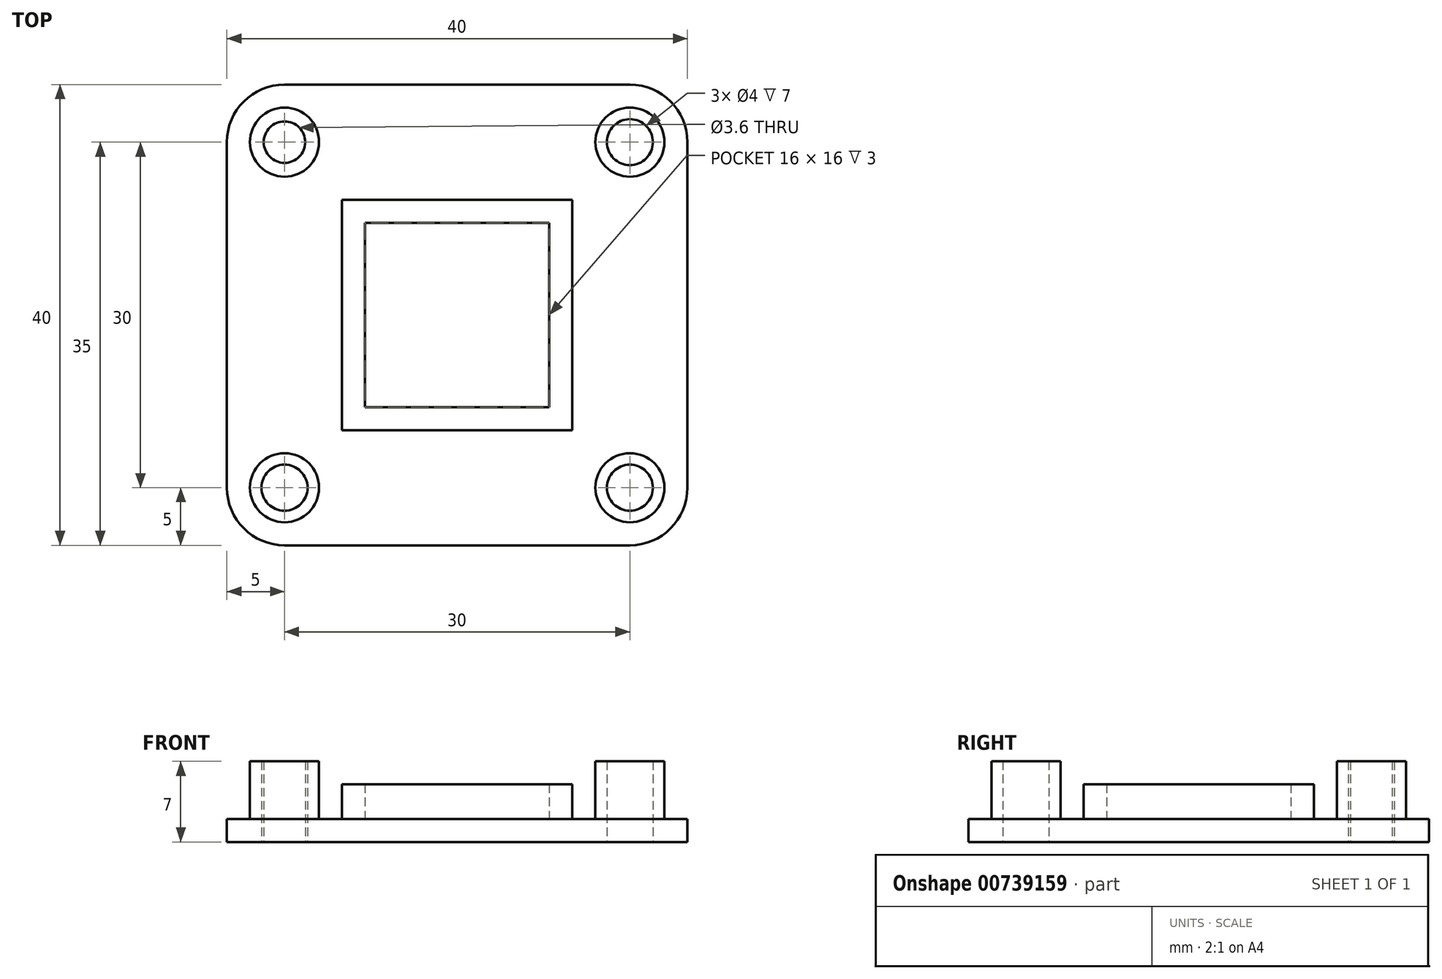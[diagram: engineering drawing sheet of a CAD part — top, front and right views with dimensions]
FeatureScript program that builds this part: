
annotation { "Feature Type Name" : "Feature", "Feature Type Description" : "" }
export const myFeature = defineFeature(function(context is Context, id is Id, definition is map)
    precondition{}
    {
        {
            var Q0;
            Q0=qCreatedBy(makeId("Top.planeOp"),FACE);
            var sketch = newSketch(context, id + "F0", { "sketchPlane" : qUnion([Q0])});
            skLineSegment(sketch, "E0.bottom", {"start": v(15, -20) * mm, "end": v(-15, -20) * mm});
            skLineSegment(sketch, "E0.top", {"start": v(15, 20) * mm, "end": v(-15, 20) * mm});
            skLineSegment(sketch, "E0.left", {"start": v(20, -15) * mm, "end": v(20, 15) * mm});
            skLineSegment(sketch, "E0.right", {"start": v(-20, -15) * mm, "end": v(-20, 15) * mm});
            skPoint(sketch, "E0.middle", {"position": v(0, 0) * mm});
            skCircle(sketch, "E1", {"center": v(-15, -15) * mm, "radius": 2 * mm});
            skCircle(sketch, "E2", {"center": v(-15, 15) * mm, "radius": 1.8 * mm});
            skCircle(sketch, "E3", {"center": v(15, -15) * mm, "radius": 2 * mm});
            skCircle(sketch, "E4", {"center": v(15, 15) * mm, "radius": 2 * mm});
            skPoint(sketch, "E5.visualSharp", {"position": v(-20, 20) * mm});
            skArc(sketch, "E5.filletArc", {"start": v(-15, 20) * mm, "mid": v(-18.54, 18.54) * mm, "end": v(-20, 15) * mm});
            skPoint(sketch, "E6.visualSharp", {"position": v(20, 20) * mm});
            skArc(sketch, "E6.filletArc", {"start": v(20, 15) * mm, "mid": v(18.54, 18.54) * mm, "end": v(15, 20) * mm});
            skPoint(sketch, "E7.visualSharp", {"position": v(20, -20) * mm});
            skArc(sketch, "E7.filletArc", {"start": v(15, -20) * mm, "mid": v(18.54, -18.54) * mm, "end": v(20, -15) * mm});
            skPoint(sketch, "E8.visualSharp", {"position": v(-20, -20) * mm});
            skArc(sketch, "E8.filletArc", {"start": v(-20, -15) * mm, "mid": v(-18.54, -18.54) * mm, "end": v(-15, -20) * mm});
            skSolve(sketch);
        }
        {
            var Q0;
            Q0=makeQuery(id+"F0.imprint","IMPRINT",FACE,{"disambiguationData":[TD([[makeQuery(id+"F0.imprint","IMPRINT",EDGE,{"derivedFrom":sQuery(id+"F0.wireOp",EDGE,"E0.bottom")}),-1.0]])]});
            var Q1;
            Q1=makeQuery(id+"F0.imprint","IMPRINT",FACE,{"disambiguationData":[TD([[makeQuery(id+"F0.imprint","IMPRINT",EDGE,{"derivedFrom":sQuery(id+"F0.wireOp",EDGE,"E4")}),-1.0]])]});
            var Q2;
            Q2=makeQuery(id+"F0.imprint","IMPRINT",FACE,{"disambiguationData":[TD([[makeQuery(id+"F0.imprint","IMPRINT",EDGE,{"derivedFrom":sQuery(id+"F0.wireOp",EDGE,"E2")}),-1.0]])]});
            var Q3;
            Q3=makeQuery(id+"F0.imprint","IMPRINT",FACE,{"disambiguationData":[TD([[makeQuery(id+"F0.imprint","IMPRINT",EDGE,{"derivedFrom":sQuery(id+"F0.wireOp",EDGE,"E1")}),-1.0]])]});
            var Q4;
            Q4=makeQuery(id+"F0.imprint","IMPRINT",FACE,{"disambiguationData":[TD([[makeQuery(id+"F0.imprint","IMPRINT",EDGE,{"derivedFrom":sQuery(id+"F0.wireOp",EDGE,"E3")}),-1.0]])]});
            extrude(context, id + "F1", {"entities" : qUnion([Q0, Q1, Q2, Q3, Q4]), "depth" : 2 * mm, "offsetDistance" : 25 * mm});
        }
        {
            var Q0;
            Q0=makeQuery(id+"F1.opExtrude","CAP_FACE",FACE,{"disambiguationData":[OSD([sQuery(id+"F0.wireOp",EDGE,"E0.bottom"),sQuery(id+"F0.wireOp",EDGE,"E0.top"),sQuery(id+"F0.wireOp",EDGE,"E0.left"),sQuery(id+"F0.wireOp",EDGE,"E0.right"),sQuery(id+"F0.wireOp",EDGE,"E1"),sQuery(id+"F0.wireOp",EDGE,"E2"),sQuery(id+"F0.wireOp",EDGE,"E3"),sQuery(id+"F0.wireOp",EDGE,"E4")])],"isStart":false});
            var sketch = newSketch(context, id + "F2", { "sketchPlane" : qUnion([Q0])});
            skCircle(sketch, "E9.0", {"center": v(-15, 15) * mm, "radius": 1.8 * mm});
            skCircle(sketch, "E9.1", {"center": v(15, 15) * mm, "radius": 2 * mm});
            skCircle(sketch, "E9.2", {"center": v(15, -15) * mm, "radius": 2 * mm});
            skCircle(sketch, "E9.3", {"center": v(-15, -15) * mm, "radius": 2 * mm});
            skCircle(sketch, "E10", {"center": v(-15, 15) * mm, "radius": 3 * mm});
            skCircle(sketch, "E11", {"center": v(15, 15) * mm, "radius": 3 * mm});
            skCircle(sketch, "E12", {"center": v(15, -15) * mm, "radius": 3 * mm});
            skCircle(sketch, "E13", {"center": v(-15, -15) * mm, "radius": 3 * mm});
            skSolve(sketch);
        }
        {
            var Q0;
            Q0=makeQuery(id+"F2.imprint","IMPRINT",FACE,{"disambiguationData":[TD([[makeQuery(id+"F2.imprint","IMPRINT",EDGE,{"derivedFrom":sQuery(id+"F2.wireOp",EDGE,"E9.0")}),-1.0]])]});
            var Q1;
            Q1=makeQuery(id+"F2.imprint","IMPRINT",FACE,{"disambiguationData":[TD([[makeQuery(id+"F2.imprint","IMPRINT",EDGE,{"derivedFrom":sQuery(id+"F2.wireOp",EDGE,"E9.1")}),-1.0]])]});
            var Q2;
            Q2=makeQuery(id+"F2.imprint","IMPRINT",FACE,{"disambiguationData":[TD([[makeQuery(id+"F2.imprint","IMPRINT",EDGE,{"derivedFrom":sQuery(id+"F2.wireOp",EDGE,"E9.2")}),-1.0]])]});
            var Q3;
            Q3=makeQuery(id+"F2.imprint","IMPRINT",FACE,{"disambiguationData":[TD([[makeQuery(id+"F2.imprint","IMPRINT",EDGE,{"derivedFrom":sQuery(id+"F2.wireOp",EDGE,"E9.3")}),-1.0]])]});
            extrude(context, id + "F3", {"entities" : qUnion([Q0, Q1, Q2, Q3]), "operationType" : NewBodyOperationType.ADD, "depth" : 5 * mm, "offsetDistance" : 25 * mm});
        }
        {
            var Q0;
            Q0=makeQuery(id+"F1.opExtrude","CAP_FACE",FACE,{"disambiguationData":[OSD([sQuery(id+"F0.wireOp",EDGE,"E0.bottom"),sQuery(id+"F0.wireOp",EDGE,"E0.top"),sQuery(id+"F0.wireOp",EDGE,"E0.left"),sQuery(id+"F0.wireOp",EDGE,"E0.right"),sQuery(id+"F0.wireOp",EDGE,"E1"),sQuery(id+"F0.wireOp",EDGE,"E2"),sQuery(id+"F0.wireOp",EDGE,"E3"),sQuery(id+"F0.wireOp",EDGE,"E4"),sQuery(id+"F0.wireOp",EDGE,"E5.filletArc"),sQuery(id+"F0.wireOp",EDGE,"E6.filletArc"),sQuery(id+"F0.wireOp",EDGE,"E7.filletArc"),sQuery(id+"F0.wireOp",EDGE,"E8.filletArc")])],"isStart":false});
            var sketch = newSketch(context, id + "F4", { "sketchPlane" : qUnion([Q0])});
            skLineSegment(sketch, "E14.bottom", {"start": v(8, -8) * mm, "end": v(-8, -8) * mm});
            skLineSegment(sketch, "E14.top", {"start": v(8, 8) * mm, "end": v(-8, 8) * mm});
            skLineSegment(sketch, "E14.left", {"start": v(8, -8) * mm, "end": v(8, 8) * mm});
            skLineSegment(sketch, "E14.right", {"start": v(-8, -8) * mm, "end": v(-8, 8) * mm});
            skPoint(sketch, "E14.middle", {"position": v(0, 0) * mm});
            skLineSegment(sketch, "E15.bottom", {"start": v(10, -10) * mm, "end": v(-10, -10) * mm});
            skLineSegment(sketch, "E15.top", {"start": v(10, 10) * mm, "end": v(-10, 10) * mm});
            skLineSegment(sketch, "E15.left", {"start": v(10, -10) * mm, "end": v(10, 10) * mm});
            skLineSegment(sketch, "E15.right", {"start": v(-10, -10) * mm, "end": v(-10, 10) * mm});
            skSolve(sketch);
        }
        {
            var Q0;
            Q0=makeQuery(id+"F4.imprint","IMPRINT",FACE,{"disambiguationData":[TD([[makeQuery(id+"F4.imprint","IMPRINT",EDGE,{"derivedFrom":sQuery(id+"F4.wireOp",EDGE,"E14.bottom")}),1.0]])]});
            extrude(context, id + "F5", {"entities" : qUnion([Q0]), "operationType" : NewBodyOperationType.ADD, "depth" : 3 * mm, "offsetDistance" : 25 * mm});
        }
    });
